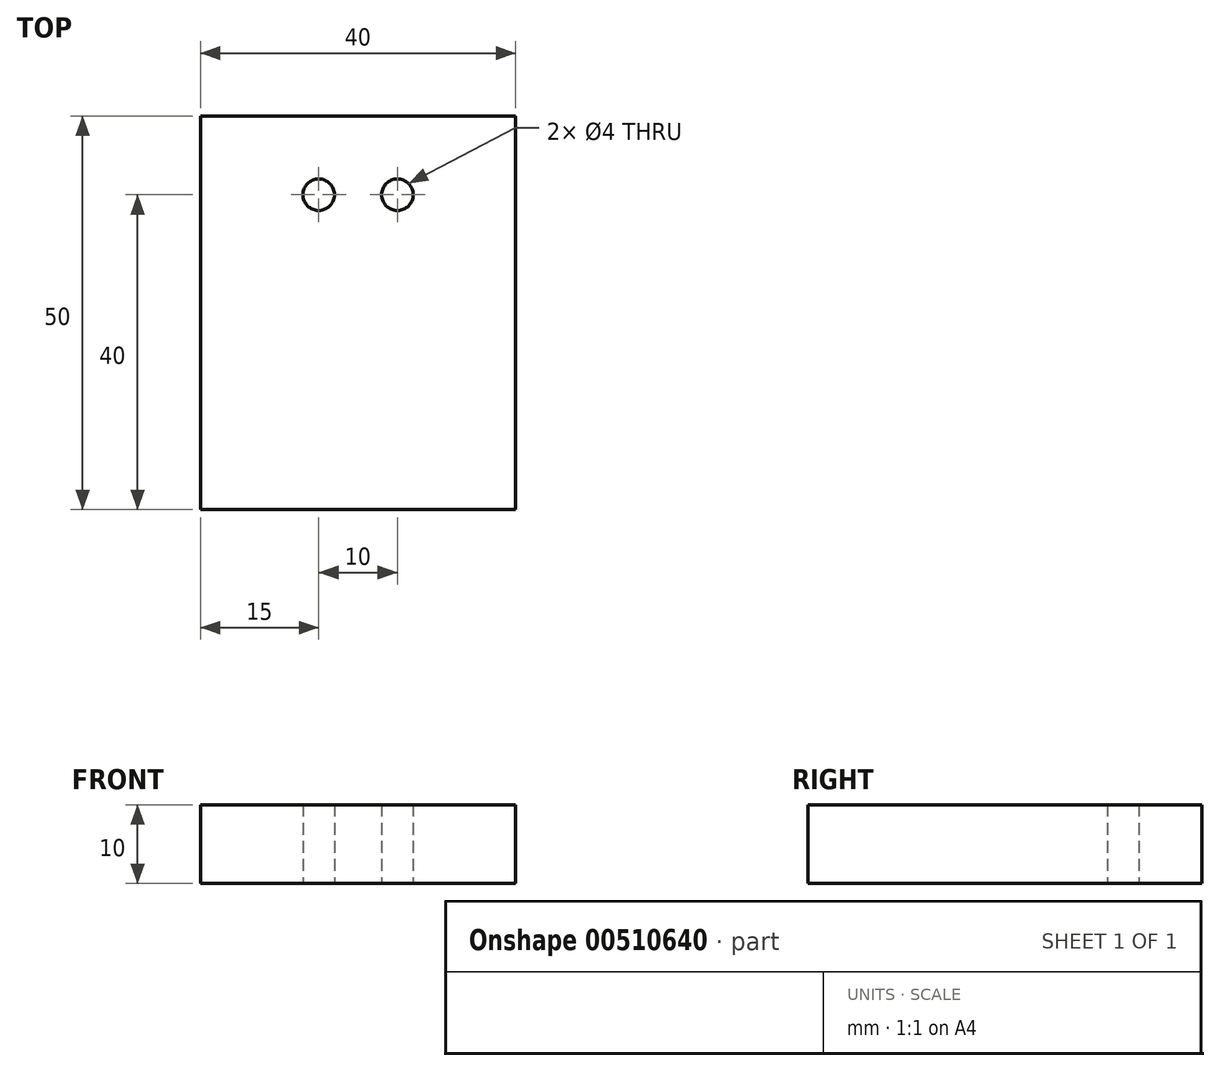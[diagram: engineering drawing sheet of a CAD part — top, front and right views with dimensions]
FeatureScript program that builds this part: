
annotation { "Feature Type Name" : "Feature", "Feature Type Description" : "" }
export const myFeature = defineFeature(function(context is Context, id is Id, definition is map)
    precondition{}
    {
        {
            var Q0;
            Q0=qCreatedBy(makeId("Top.planeOp"),FACE);
            var sketch = newSketch(context, id + "F0", { "sketchPlane" : qUnion([Q0])});
            skLineSegment(sketch, "E0.bottom", {"start": v(-20, 25) * mm, "end": v(20, 25) * mm});
            skLineSegment(sketch, "E0.top", {"start": v(-20, -25) * mm, "end": v(20, -25) * mm});
            skLineSegment(sketch, "E0.left", {"start": v(-20, 25) * mm, "end": v(-20, -25) * mm});
            skLineSegment(sketch, "E0.right", {"start": v(20, 25) * mm, "end": v(20, -25) * mm});
            skPoint(sketch, "E0.middle", {"position": v(0, 0) * mm});
            skCircle(sketch, "E1", {"center": v(-5, 15) * mm, "radius": 2 * mm});
            skCircle(sketch, "E2", {"center": v(5, 15) * mm, "radius": 2 * mm});
            skSolve(sketch);
        }
        {
            var Q0;
            Q0=makeQuery(id+"F0.imprint","IMPRINT",FACE,{"disambiguationData":[TD([[makeQuery(id+"F0.imprint","IMPRINT",EDGE,{"derivedFrom":sQuery(id+"F0.wireOp",EDGE,"E0.bottom")}),-1.0]])]});
            extrude(context, id + "F1", {"entities" : qUnion([Q0]), "depth" : 10 * mm});
        }
    });
